# Revit family: Unterlegscheibe DIN EN ISO 7089, fvz
name_source: partatom
category: HLS-Bauteile
revit_build: Autodesk Revit 2017 (Build: 20190507_1515(x64)
units: mm (PartAtom-declared; Revit-internal decimal feet)

## family parameters
Arbeitsebenenbasiert = Ja
Beim Laden mit Abzugskörper schneiden = Nein
Bemaßung runder Anschluss = Durchmesser verwenden
Gemeinsam genutzt = Ja
Immer vertikal = Nein
Raumberechnungspunkt = Nein
Teiletyp = Normal

## types (3) — shared parameters
Fabrikat = MEFA
Firma = MEFA Befestigungs- und Montagesysteme GmbH
Kurztext1 = Unterlegscheibe
L = 3 mm  [stored 0.00984252 ft]
Material = Stahl
Mengeneinheit = St
Vorgabe-Ansicht = 1219 mm
vpe = 100 St

## per-type parameters (varying)
| type | Artikelnummer | D | D0 | EAN | Gewicht | Gewicht pro Bauteil | Kurztext2 |
| Unterlegscheibe 13x 24x 2,5, fvz | 4320271/fvz | 24 mm  [stored 0.0787402 ft] | 13 mm | 4250928454782 | 0.01 kg | 0.01 kg | 13 x 24 x 2,5 mm fvz |
| Unterlegscheibe 13x 37x 3,0, fvz | 4330277/fvz | 37 mm  [stored 0.121391 ft] | 13 mm | 4250928457189 | 0.02 kg | 0.02 kg | 13 x 37 x 3 mm fvz |
| Unterlegscheibe 17x 50x 3,0, fvz | 4330285/fvz | 50 mm  [stored 0.164042 ft] | 17 mm | 4250928457196 | 0.04 kg | 0.04 kg | 17 x 50 x 3 mm fvz |

note: [stored X ft] marks values corroborated as IEEE doubles in the binary element streams (Revit-internal decimal feet)
